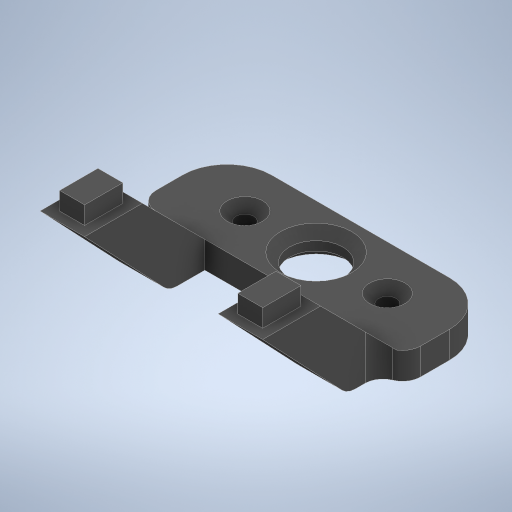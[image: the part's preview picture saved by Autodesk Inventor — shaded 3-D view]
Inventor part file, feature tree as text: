
AUTODESK INVENTOR PART (.ipt)
format: ipt  version: 2024.2 (Build 282272000, 272)  size: 352,256 bytes
history: native  units: mm
features: extrude x5, sketch x5, fillet x4, chamfer x3, plane x2, mirror x1
ambient origin geometry x8: Origin, YZ Plane, XZ Plane, XY Plane, X Axis, Y Axis, Z Axis, Center Point
bodies: Solid1 (feature_tree)
feature tree (20):
  extrude  "Extrusion1"  Depth=10.0mm
  plane  "Work Plane2"
  extrude  "Extrusion3"  [1 undecoded]
  plane  "Work Plane3"
  fillet  "Fillet2"  Radius=4.0mm
  fillet  "Fillet3"  Radius=6.5mm
  fillet  "Fillet4"  [1 undecoded]
  extrude  "Extrusion4"  Depth=5.0mm TaperAngle=0.0deg
  mirror  "Mirror2"
  extrude  "Extrusion5"  Depth=2.0mm
  chamfer  "Chamfer1"  Distance=2.8mm
  extrude  "Extrusion6"  Depth=4.3mm
  chamfer  "Chamfer2"  Distance=1.1mm
  fillet  "Fillet5"  Radius=1.1mm
  chamfer  "Chamfer3"  Distance=2.0mm
  sketch  "Sketch1"  dims[d0=30.0mm d1=10.0mm]
  sketch  "Sketch3"  dims[d2=3.0mm d3=0.0mm d12=-2.5mm d13=4.0mm d14=6.5mm d15=45.0deg]
  sketch  "Sketch5"  dims[d16=10.0mm d17=5.0mm d18=0.0mm]
  sketch  "Sketch6"  dims[d19=-15.0mm d20=2.0mm d21=2.0mm]
  sketch  "Sketch7"  dims[d22=5.0mm d26=2.8mm d27=4.3mm d28=1.1mm d29=1.1mm d30=2.0mm d31=0.0mm d32=6.0mm d33=5.0mm d34=15.0mm d35=0.0mm d36=0.0mm d37=1.0mm d38=2.0mm d39=45.0deg d40=2.0mm d41=2.0mm d42=5.0mm d43=5.0mm d44=8.0mm d45=8.0mm d46=0.0mm d47=0.0mm d48=1.0mm d49=2.0mm d50=45.0deg d51=2.0mm d52=1.0mm d53=2.0mm d54=45.0deg]
note: 2 required parameter values undecoded (feature->parameter linkage not recoverable at this tier; creation-order binding heuristic only, values carry confidence <= 0.55)
